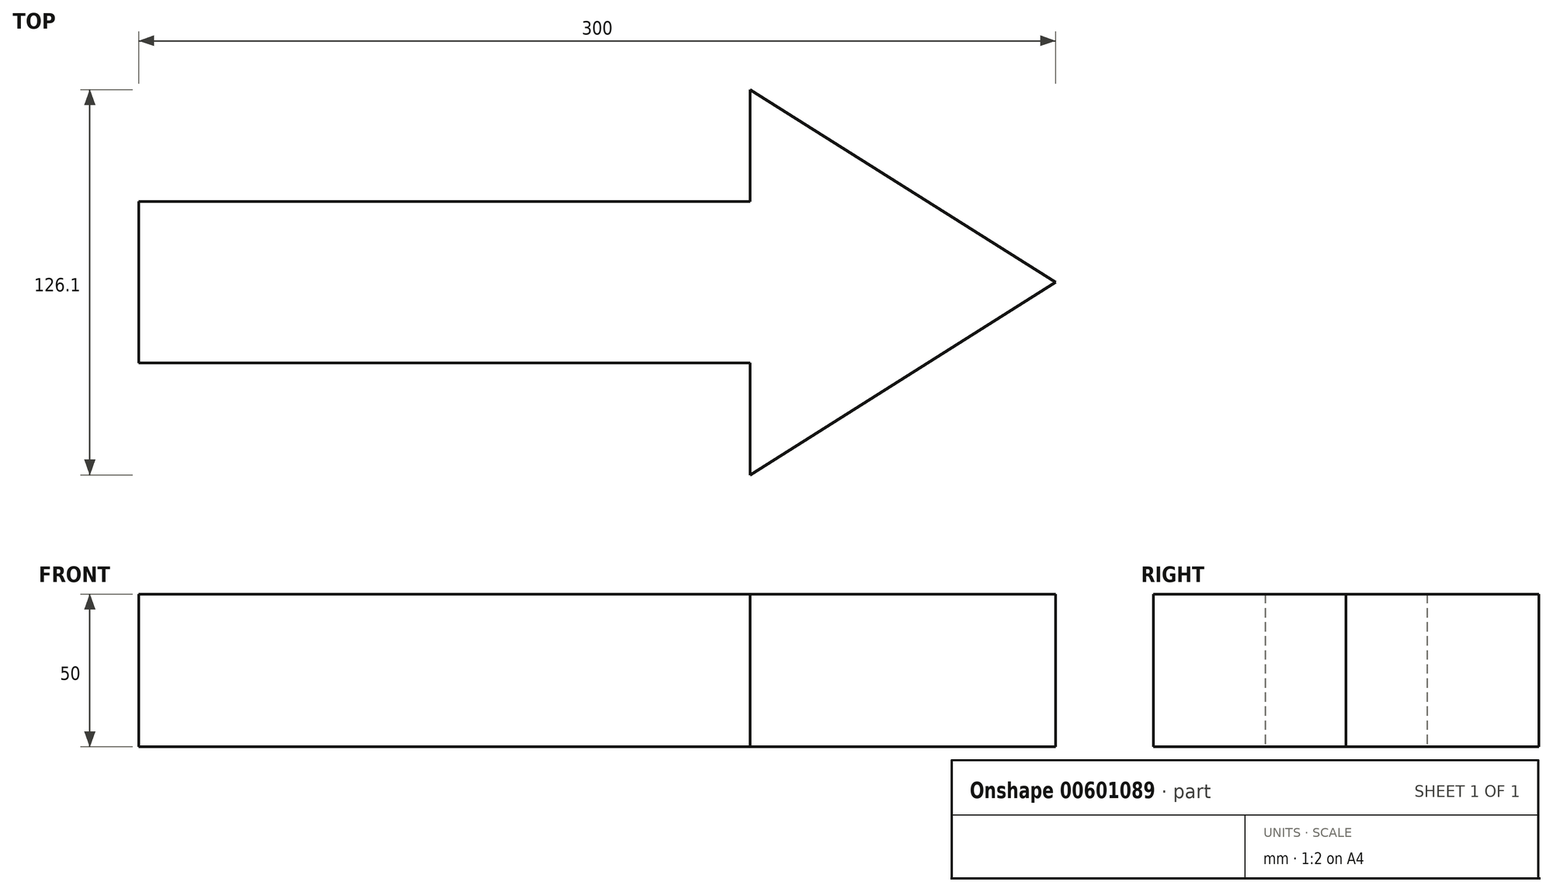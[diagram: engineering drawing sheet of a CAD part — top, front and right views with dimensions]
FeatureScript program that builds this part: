
annotation { "Feature Type Name" : "Feature", "Feature Type Description" : "" }
export const myFeature = defineFeature(function(context is Context, id is Id, definition is map)
    precondition{}
    {
        {
            var Q0;
            Q0=qCreatedBy(makeId("Top.planeOp"),FACE);
            var sketch = newSketch(context, id + "F0", { "sketchPlane" : qUnion([Q0])});
            skLineSegment(sketch, "E0", {"start": v(0, 0) * mm, "end": v(-100, 63.05) * mm});
            skLineSegment(sketch, "E1", {"start": v(-100, 63.05) * mm, "end": v(-100, 26.44) * mm});
            skLineSegment(sketch, "E2", {"start": v(-100, 26.44) * mm, "end": v(-300, 26.44) * mm});
            skLineSegment(sketch, "E3", {"start": v(-300, 26.44) * mm, "end": v(-300, 0) * mm});
            skLineSegment(sketch, "E4", {"start": v(-300, 0) * mm, "end": v(0, 0) * mm});
            skLineSegment(sketch, "E5.MirrorCS", {"start": v(-300, -26.44) * mm, "end": v(-300, 0) * mm});
            skLineSegment(sketch, "E6.MirrorCS", {"start": v(-100, -26.44) * mm, "end": v(-300, -26.44) * mm});
            skLineSegment(sketch, "E7.MirrorCS", {"start": v(0, 0) * mm, "end": v(-100, -63.05) * mm});
            skLineSegment(sketch, "E8.MirrorCS", {"start": v(-100, -63.05) * mm, "end": v(-100, -26.44) * mm});
            skSolve(sketch);
        }
        {
            var Q0;
            Q0=makeQuery(id+"F0.imprint","IMPRINT",FACE,{"disambiguationData":[TD([[makeQuery(id+"F0.imprint","IMPRINT",EDGE,{"derivedFrom":sQuery(id+"F0.wireOp",EDGE,"E0")}),1.0]])]});
            var Q1;
            Q1=makeQuery(id+"F0.imprint","IMPRINT",FACE,{"disambiguationData":[TD([[makeQuery(id+"F0.imprint","IMPRINT",EDGE,{"derivedFrom":sQuery(id+"F0.wireOp",EDGE,"E4")}),-1.0]])]});
            extrude(context, id + "F1", {"entities" : qUnion([Q0, Q1]), "depth" : 50 * mm, "offsetDistance" : 25 * mm});
        }
    });
